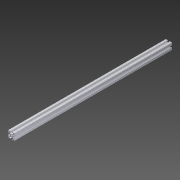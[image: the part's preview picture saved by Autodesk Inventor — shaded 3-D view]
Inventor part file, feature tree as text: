
AUTODESK INVENTOR PART (.ipt)
format: ipt  version: 2013 (Build 170138000, 138)  size: 291,840 bytes
history: native  units: in
note: dims shown in document units (in); Inventor stores cm internally (conversion verified against a paired STEP export)
features: extrude x2, imported_body x1, sketch x1
ambient origin geometry x8: Origin, YZ Plane, XZ Plane, XY Plane, X Axis, Y Axis, Z Axis, Center Point
feature tree (4):
  extrude  "Extrude1"  [1 undecoded]
  extrude  "Extrusion1"  [1 undecoded]
  imported_body  "Base1"
  sketch  "Sketch1"  dims[d0=12.0in d1=0.0in]
note: 2 required parameter values undecoded (feature->parameter linkage not recoverable at this tier; creation-order binding heuristic only, values carry confidence <= 0.55)
